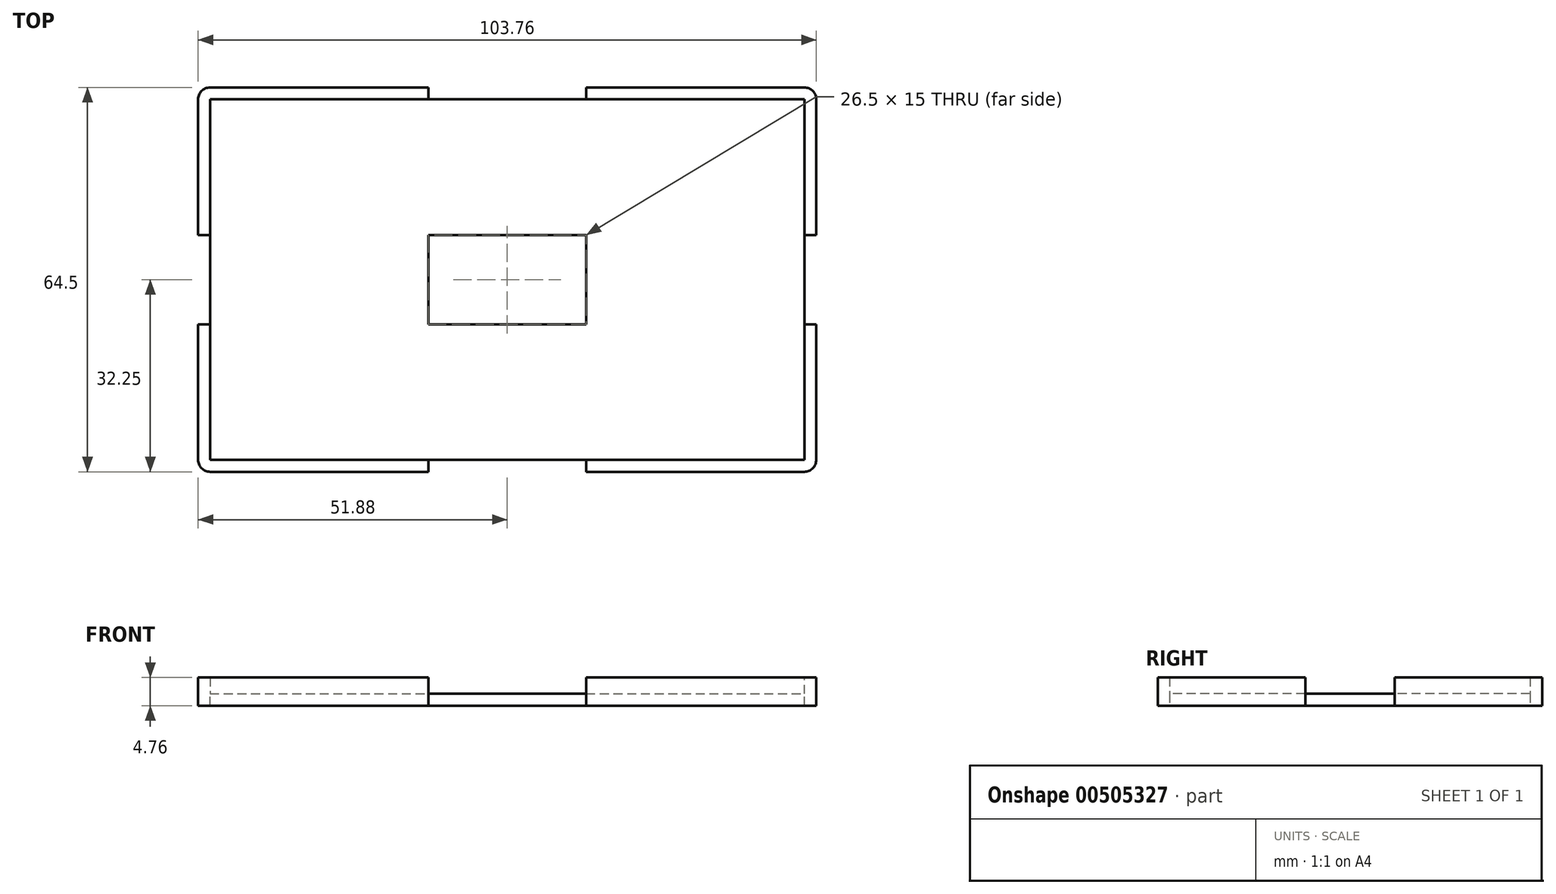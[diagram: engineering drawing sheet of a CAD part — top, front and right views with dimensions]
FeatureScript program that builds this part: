
annotation { "Feature Type Name" : "Feature", "Feature Type Description" : "" }
export const myFeature = defineFeature(function(context is Context, id is Id, definition is map)
    precondition{}
    {
        {
            var Q0;
            Q0=qCreatedBy(makeId("Top.planeOp"),FACE);
            var sketch = newSketch(context, id + "F0", { "sketchPlane" : qUnion([Q0])});
            skLineSegment(sketch, "E0.bottom", {"start": v(-51.88, 32.25) * mm, "end": v(51.88, 32.25) * mm});
            skLineSegment(sketch, "E0.top", {"start": v(-51.88, -32.25) * mm, "end": v(51.88, -32.25) * mm});
            skLineSegment(sketch, "E0.left", {"start": v(-51.88, 32.25) * mm, "end": v(-51.88, -32.25) * mm});
            skLineSegment(sketch, "E0.right", {"start": v(51.88, 32.25) * mm, "end": v(51.88, -32.25) * mm});
            skPoint(sketch, "E0.middle", {"position": v(0, 0) * mm});
            skSolve(sketch);
        }
        {
            var Q0;
            Q0=makeQuery(id+"F0.imprint","IMPRINT",FACE,{"disambiguationData":[TD([[makeQuery(id+"F0.imprint","IMPRINT",EDGE,{"derivedFrom":sQuery(id+"F0.wireOp",EDGE,"E0.bottom")}),-1.0]])]});
            extrude(context, id + "F1", {"entities" : qUnion([Q0]), "endBound" : BoundingType.SYMMETRIC, "depth" : 4.75 * mm});
        }
        {
            var Q0;
            Q0=makeQuery(id+"F1.opExtrude","CAP_FACE",FACE,{"disambiguationData":[OSD([sQuery(id+"F0.wireOp",EDGE,"E0.bottom"),sQuery(id+"F0.wireOp",EDGE,"E0.top"),sQuery(id+"F0.wireOp",EDGE,"E0.left"),sQuery(id+"F0.wireOp",EDGE,"E0.right")])],"isStart":false});
            shell(context, id + "F2", {"entities" : qUnion([Q0]), "thickness" : 2 * mm});
        }
        {
            var Q0;
            Q0=qCreatedBy(makeId("Top.planeOp"),FACE);
            var sketch = newSketch(context, id + "F3", { "sketchPlane" : qUnion([Q0])});
            skLineSegment(sketch, "E1.bottom", {"start": v(13.25, -7.5) * mm, "end": v(-13.25, -7.5) * mm});
            skLineSegment(sketch, "E1.top", {"start": v(13.25, 7.5) * mm, "end": v(-13.25, 7.5) * mm});
            skLineSegment(sketch, "E1.left", {"start": v(13.25, -7.5) * mm, "end": v(13.25, 7.5) * mm});
            skLineSegment(sketch, "E1.right", {"start": v(-13.25, -7.5) * mm, "end": v(-13.25, 7.5) * mm});
            skPoint(sketch, "E1.middle", {"position": v(0, 0) * mm});
            skSolve(sketch);
        }
        {
            var Q0;
            Q0 = qSketchRegion(id + "F3", true);
            extrude(context, id + "F4", {"entities" : qUnion([Q0]), "operationType" : NewBodyOperationType.REMOVE, "endBound" : BoundingType.SYMMETRIC, "oppositeDirection" : true, "depth" : 25.4 * mm});
        }
        {
            var Q0;
            Q0=qCreatedBy(makeId("Top.planeOp"),FACE);
            var sketch = newSketch(context, id + "F5", { "sketchPlane" : qUnion([Q0])});
            skLineSegment(sketch, "E2.bottom", {"start": v(-13.25, -32.45) * mm, "end": v(13.25, -32.45) * mm});
            skLineSegment(sketch, "E2.top", {"start": v(-13.25, -30.25) * mm, "end": v(13.25, -30.25) * mm});
            skLineSegment(sketch, "E2.left", {"start": v(-13.25, -32.45) * mm, "end": v(-13.25, -30.25) * mm});
            skLineSegment(sketch, "E2.right", {"start": v(13.25, -32.45) * mm, "end": v(13.25, -30.25) * mm});
            skSolve(sketch);
        }
        {
            var Q0;
            Q0 = qSketchRegion(id + "F5", true);
            extrude(context, id + "F6", {"entities" : qUnion([Q0]), "operationType" : NewBodyOperationType.REMOVE, "endBound" : BoundingType.SYMMETRIC, "depth" : 25.4 * mm});
        }
        {
            var Q0;
            Q0=qCreatedBy(makeId("Top.planeOp"),FACE);
            var sketch = newSketch(context, id + "F7", { "sketchPlane" : qUnion([Q0])});
            skLineSegment(sketch, "E3.bottom", {"start": v(-13.25, 30.26) * mm, "end": v(13.25, 30.26) * mm});
            skLineSegment(sketch, "E3.top", {"start": v(-13.25, 32.46) * mm, "end": v(13.25, 32.46) * mm});
            skLineSegment(sketch, "E3.left", {"start": v(-13.25, 30.26) * mm, "end": v(-13.25, 32.46) * mm});
            skLineSegment(sketch, "E3.right", {"start": v(13.25, 30.26) * mm, "end": v(13.25, 32.46) * mm});
            skSolve(sketch);
        }
        {
            var Q0;
            Q0 = qSketchRegion(id + "F7", true);
            extrude(context, id + "F8", {"entities" : qUnion([Q0]), "operationType" : NewBodyOperationType.REMOVE, "endBound" : BoundingType.SYMMETRIC, "depth" : 25.4 * mm});
        }
        {
            var Q0;
            Q0=qCreatedBy(makeId("Top.planeOp"),FACE);
            var sketch = newSketch(context, id + "F9", { "sketchPlane" : qUnion([Q0])});
            skLineSegment(sketch, "E4.bottom", {"start": v(-52.08, -7.52) * mm, "end": v(-49.88, -7.52) * mm});
            skLineSegment(sketch, "E4.top", {"start": v(-52.08, 7.48) * mm, "end": v(-49.88, 7.48) * mm});
            skLineSegment(sketch, "E4.left", {"start": v(-52.08, -7.52) * mm, "end": v(-52.08, 7.48) * mm});
            skLineSegment(sketch, "E4.right", {"start": v(-49.88, -7.52) * mm, "end": v(-49.88, 7.48) * mm});
            skSolve(sketch);
        }
        {
            var Q0;
            Q0 = qSketchRegion(id + "F9", true);
            extrude(context, id + "F10", {"entities" : qUnion([Q0]), "operationType" : NewBodyOperationType.REMOVE, "endBound" : BoundingType.SYMMETRIC, "oppositeDirection" : true, "depth" : 25.4 * mm});
        }
        {
            var Q0;
            Q0=qCreatedBy(makeId("Top.planeOp"),FACE);
            var sketch = newSketch(context, id + "F11", { "sketchPlane" : qUnion([Q0])});
            skLineSegment(sketch, "E5.bottom", {"start": v(49.88, -7.5) * mm, "end": v(52.08, -7.5) * mm});
            skLineSegment(sketch, "E5.top", {"start": v(49.88, 7.5) * mm, "end": v(52.08, 7.5) * mm});
            skLineSegment(sketch, "E5.left", {"start": v(49.88, -7.5) * mm, "end": v(49.88, 7.5) * mm});
            skLineSegment(sketch, "E5.right", {"start": v(52.08, -7.5) * mm, "end": v(52.08, 7.5) * mm});
            skSolve(sketch);
        }
        {
            var Q0;
            Q0 = qSketchRegion(id + "F11", true);
            extrude(context, id + "F12", {"entities" : qUnion([Q0]), "operationType" : NewBodyOperationType.REMOVE, "endBound" : BoundingType.SYMMETRIC, "oppositeDirection" : true, "depth" : 25.4 * mm});
        }
        {
            var Q0;
            Q0=makeQuery(id+"F1.opExtrude","SWEPT_EDGE",EDGE,{"disambiguationData":[OSD([sQuery(id+"F0.wireOp",EDGE,"E0.bottom"),sQuery(id+"F0.wireOp",EDGE,"E0.left")])]});
            fillet(context, id + "F13", {"entities" : qUnion([Q0]), "radius" : 2 * mm, "tangentPropagation" : true, "allowEdgeOverflow" : false});
        }
        {
            var Q0;
            Q0=makeQuery(id+"F1.opExtrude","SWEPT_EDGE",EDGE,{"disambiguationData":[OSD([sQuery(id+"F0.wireOp",EDGE,"E0.top"),sQuery(id+"F0.wireOp",EDGE,"E0.left")])]});
            var Q1;
            Q1=makeQuery(id+"F1.opExtrude","SWEPT_EDGE",EDGE,{"disambiguationData":[OSD([sQuery(id+"F0.wireOp",EDGE,"E0.top"),sQuery(id+"F0.wireOp",EDGE,"E0.right")])]});
            var Q2;
            Q2=makeQuery(id+"F1.opExtrude","SWEPT_EDGE",EDGE,{"disambiguationData":[OSD([sQuery(id+"F0.wireOp",EDGE,"E0.bottom"),sQuery(id+"F0.wireOp",EDGE,"E0.right")])]});
            fillet(context, id + "F14", {"entities" : qUnion([Q0, Q1, Q2]), "radius" : 2 * mm, "tangentPropagation" : true, "allowEdgeOverflow" : false});
        }
    });
